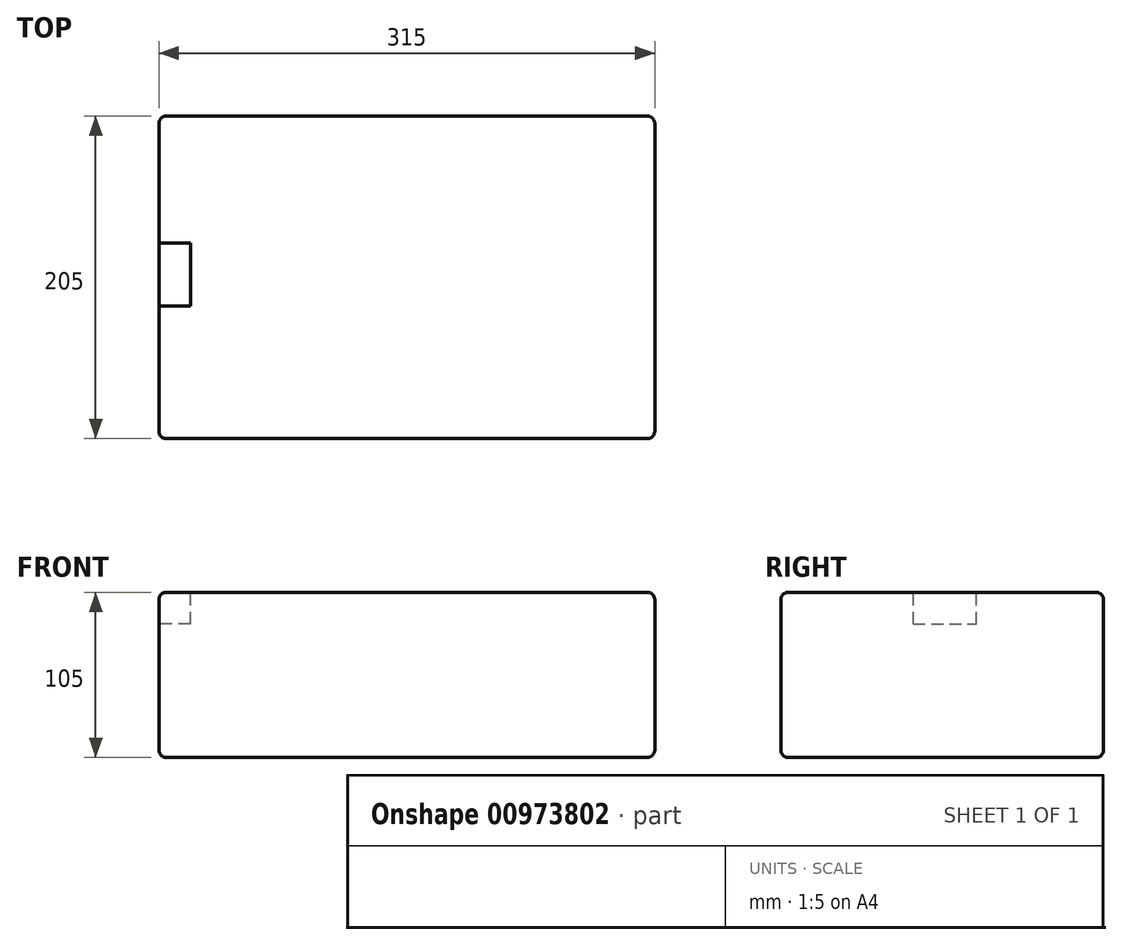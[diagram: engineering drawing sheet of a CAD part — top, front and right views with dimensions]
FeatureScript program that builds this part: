
annotation { "Feature Type Name" : "Feature", "Feature Type Description" : "" }
export const myFeature = defineFeature(function(context is Context, id is Id, definition is map)
    precondition{}
    {
        {
            var Q0;
            Q0=qCreatedBy(makeId("Top.planeOp"),FACE);
            var sketch = newSketch(context, id + "F0", { "sketchPlane" : qUnion([Q0])});
            skLineSegment(sketch, "E0.bottom", {"start": v(-157.5, -104.2) * mm, "end": v(157.5, -104.2) * mm});
            skLineSegment(sketch, "E0.top", {"start": v(-157.5, 100.8) * mm, "end": v(157.5, 100.8) * mm});
            skLineSegment(sketch, "E0.left", {"start": v(-157.5, -104.2) * mm, "end": v(-157.5, 100.8) * mm});
            skLineSegment(sketch, "E0.right", {"start": v(157.5, -104.2) * mm, "end": v(157.5, 100.8) * mm});
            skPoint(sketch, "E0.middle", {"position": v(0, -1.7) * mm});
            skSolve(sketch);
        }
        {
            var Q0;
            Q0 = qSketchRegion(id + "F0", true);
            extrude(context, id + "F1", {"entities" : qUnion([Q0]), "depth" : 105 * mm, "offsetDistance" : 25 * mm});
        }
        {
            var Q0;
            Q0=makeQuery(id+"F1.opExtrude","CAP_FACE",FACE,{"disambiguationData":[OSD([sQuery(id+"F0.wireOp",EDGE,"E0.bottom"),sQuery(id+"F0.wireOp",EDGE,"E0.top"),sQuery(id+"F0.wireOp",EDGE,"E0.left"),sQuery(id+"F0.wireOp",EDGE,"E0.right")])],"isStart":false});
            var sketch = newSketch(context, id + "F2", { "sketchPlane" : qUnion([Q0])});
            skLineSegment(sketch, "E1", {"start": v(0, 0) * mm, "end": v(-157.5, 0) * mm, "construction": true});
            skLineSegment(sketch, "E2.bottom", {"start": v(-137.5, -20) * mm, "end": v(-177.5, -20) * mm});
            skLineSegment(sketch, "E2.top", {"start": v(-137.5, 20) * mm, "end": v(-177.5, 20) * mm});
            skLineSegment(sketch, "E2.left", {"start": v(-137.5, -20) * mm, "end": v(-137.5, 20) * mm});
            skLineSegment(sketch, "E2.right", {"start": v(-177.5, -20) * mm, "end": v(-177.5, 20) * mm});
            skPoint(sketch, "E2.middle", {"position": v(-157.5, 0) * mm});
            skSolve(sketch);
        }
        {
            var Q0;
            {var subQ0=sQuery(id+"F2.wireOp",EDGE,"E2.left");Q0=makeQuery(id+"F2.imprint","IMPRINT",FACE,{"disambiguationData":[TD([[makeQuery(id+"F2.imprint","IMPRINT",EDGE,{"derivedFrom":subQ0}),1.0]])]});}
            extrude(context, id + "F3", {"entities" : qUnion([Q0]), "operationType" : NewBodyOperationType.REMOVE, "oppositeDirection" : true, "depth" : 20 * mm, "offsetDistance" : 25 * mm});
        }
        {
            var Q0;
            Q0=makeQuery(id+"F1.opExtrude","CAP_EDGE",EDGE,{"disambiguationData":[OSD([sQuery(id+"F0.wireOp",EDGE,"E0.bottom")])],"isStart":false});
            var Q1;
            Q1=makeQuery(id+"F1.opExtrude","CAP_EDGE",EDGE,{"disambiguationData":[OSD([sQuery(id+"F0.wireOp",EDGE,"E0.right")])],"isStart":false});
            var Q2;
            Q2=makeQuery(id+"F1.opExtrude","CAP_EDGE",EDGE,{"disambiguationData":[OSD([sQuery(id+"F0.wireOp",EDGE,"E0.top")])],"isStart":false});
            var Q3;
            {var subQ0=sQuery(id+"F0.wireOp",EDGE,"E0.left");var subQ1=sQuery(id+"F0.wireOp",EDGE,"E0.top");Q3=makeQuery(id+"F3.boolean.opBoolean","SPLIT",EDGE,{"disambiguationData":[TD([makeQuery(id+"F1.opExtrude","SWEPT_FACE",FACE,{"disambiguationData":[OSD([subQ1])]})])],"derivedFrom":makeQuery(id+"F1.opExtrude","CAP_EDGE",EDGE,{"disambiguationData":[OSD([subQ0])],"isStart":false})});}
            var Q4;
            {var subQ0=sQuery(id+"F0.wireOp",EDGE,"E0.bottom");var subQ1=sQuery(id+"F0.wireOp",EDGE,"E0.left");Q4=makeQuery(id+"F3.boolean.opBoolean","SPLIT",EDGE,{"disambiguationData":[TD([makeQuery(id+"F1.opExtrude","SWEPT_FACE",FACE,{"disambiguationData":[OSD([subQ0])]})])],"derivedFrom":makeQuery(id+"F1.opExtrude","CAP_EDGE",EDGE,{"disambiguationData":[OSD([subQ1])],"isStart":false})});}
            var Q5;
            Q5=makeQuery(id+"F3.boolean.opBoolean","COPY",EDGE,{"derivedFrom":makeQuery(id+"F3.opExtrude","CAP_EDGE",EDGE,{"disambiguationData":[OSD([sQuery(id+"F2.wireOp",EDGE,"E2.left")])],"isStart":true})});
            var Q6;
            Q6=makeQuery(id+"F3.boolean.opBoolean","COPY",EDGE,{"derivedFrom":makeQuery(id+"F3.opExtrude","CAP_EDGE",EDGE,{"disambiguationData":[OSD([sQuery(id+"F2.wireOp",EDGE,"E2.bottom")])],"isStart":true})});
            var Q7;
            Q7=makeQuery(id+"F3.boolean.opBoolean","COPY",EDGE,{"derivedFrom":makeQuery(id+"F3.opExtrude","CAP_EDGE",EDGE,{"disambiguationData":[OSD([sQuery(id+"F2.wireOp",EDGE,"E2.top")])],"isStart":true})});
            var Q8;
            Q8=makeQuery(id+"F1.opExtrude","SWEPT_EDGE",EDGE,{"disambiguationData":[OSD([sQuery(id+"F0.wireOp",EDGE,"E0.bottom"),sQuery(id+"F0.wireOp",EDGE,"E0.right")])]});
            var Q9;
            Q9=makeQuery(id+"F1.opExtrude","SWEPT_EDGE",EDGE,{"disambiguationData":[OSD([sQuery(id+"F0.wireOp",EDGE,"E0.top"),sQuery(id+"F0.wireOp",EDGE,"E0.right")])]});
            var Q10;
            Q10=makeQuery(id+"F1.opExtrude","CAP_EDGE",EDGE,{"disambiguationData":[OSD([sQuery(id+"F0.wireOp",EDGE,"E0.right")])],"isStart":true});
            var Q11;
            Q11=makeQuery(id+"F1.opExtrude","CAP_EDGE",EDGE,{"disambiguationData":[OSD([sQuery(id+"F0.wireOp",EDGE,"E0.bottom")])],"isStart":true});
            var Q12;
            Q12=makeQuery(id+"F1.opExtrude","SWEPT_EDGE",EDGE,{"disambiguationData":[OSD([sQuery(id+"F0.wireOp",EDGE,"E0.bottom"),sQuery(id+"F0.wireOp",EDGE,"E0.left")])]});
            var Q13;
            Q13=makeQuery(id+"F1.opExtrude","SWEPT_EDGE",EDGE,{"disambiguationData":[OSD([sQuery(id+"F0.wireOp",EDGE,"E0.top"),sQuery(id+"F0.wireOp",EDGE,"E0.left")])]});
            var Q14;
            Q14=makeQuery(id+"F1.opExtrude","CAP_EDGE",EDGE,{"disambiguationData":[OSD([sQuery(id+"F0.wireOp",EDGE,"E0.top")])],"isStart":true});
            var Q15;
            Q15=makeQuery(id+"F1.opExtrude","CAP_EDGE",EDGE,{"disambiguationData":[OSD([sQuery(id+"F0.wireOp",EDGE,"E0.left")])],"isStart":true});
            var Q16;
            Q16=makeQuery(id+"F3.boolean.opBoolean","COPY",EDGE,{"derivedFrom":makeQuery(id+"F3.opExtrude","CAP_EDGE",EDGE,{"disambiguationData":[OSD([sQuery(id+"F0.wireOp",EDGE,"E0.left")])],"isStart":false})});
            var Q17;
            Q17=makeQuery(id+"F3.boolean.opBoolean","COPY",EDGE,{"derivedFrom":makeQuery(id+"F3.opExtrude","SWEPT_EDGE",EDGE,{"disambiguationData":[OSD([sQuery(id+"F0.wireOp",EDGE,"E0.left"),sQuery(id+"F2.wireOp",EDGE,"E2.top")])]})});
            var Q18;
            Q18=makeQuery(id+"F3.boolean.opBoolean","COPY",EDGE,{"derivedFrom":makeQuery(id+"F3.opExtrude","SWEPT_EDGE",EDGE,{"disambiguationData":[OSD([sQuery(id+"F0.wireOp",EDGE,"E0.left"),sQuery(id+"F2.wireOp",EDGE,"E2.bottom")])]})});
            fillet(context, id + "F4", {"entities" : qUnion([Q0, Q1, Q2, Q3, Q4, Q5, Q6, Q7, Q8, Q9, Q10, Q11, Q12, Q13, Q14, Q15, Q16, Q17, Q18]), "radius" : 5 * mm, "tangentPropagation" : true, "allowEdgeOverflow" : false});
        }
    });
